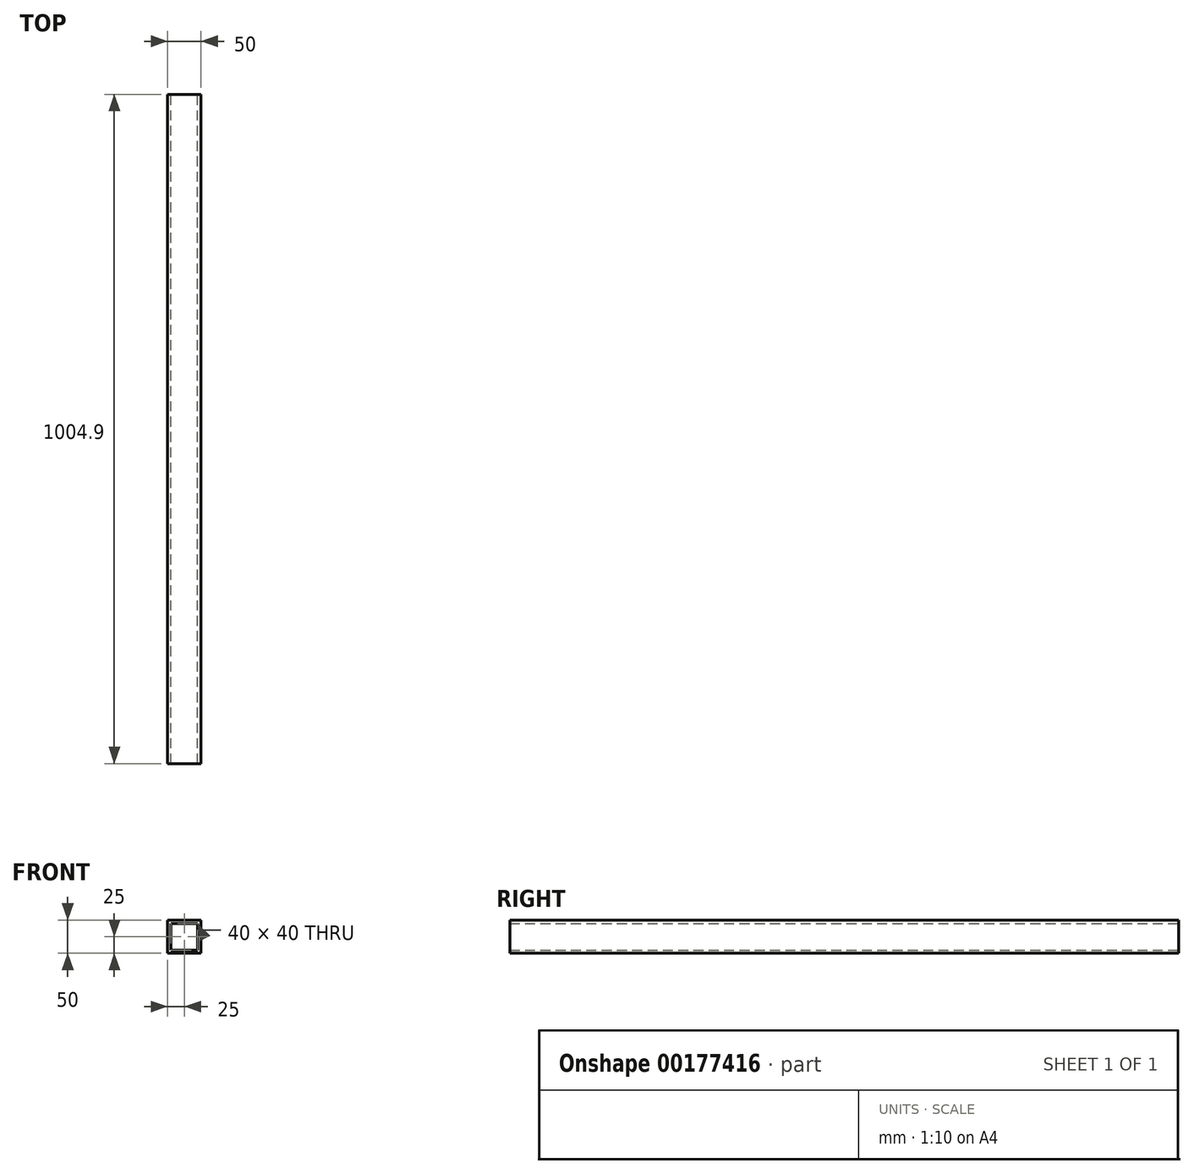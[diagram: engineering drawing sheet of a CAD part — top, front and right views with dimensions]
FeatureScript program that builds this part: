
annotation { "Feature Type Name" : "Feature", "Feature Type Description" : "" }
export const myFeature = defineFeature(function(context is Context, id is Id, definition is map)
    precondition{}
    {
        {
            var Q0;
            Q0=qCreatedBy(makeId("Front.planeOp"),FACE);
            var sketch = newSketch(context, id + "F0", { "sketchPlane" : qUnion([Q0])});
            skLineSegment(sketch, "E0.bottom", {"start": v(25, -25) * mm, "end": v(-25, -25) * mm});
            skLineSegment(sketch, "E0.top", {"start": v(25, 25) * mm, "end": v(-25, 25) * mm});
            skLineSegment(sketch, "E0.left", {"start": v(25, -25) * mm, "end": v(25, 25) * mm});
            skLineSegment(sketch, "E0.right", {"start": v(-25, -25) * mm, "end": v(-25, 25) * mm});
            skPoint(sketch, "E0.middle", {"position": v(0, 0) * mm});
            skLineSegment(sketch, "E1.0", {"start": v(20, 20) * mm, "end": v(-20, 20) * mm});
            skLineSegment(sketch, "E1.1", {"start": v(20, -20) * mm, "end": v(20, 20) * mm});
            skLineSegment(sketch, "E1.2", {"start": v(20, -20) * mm, "end": v(-20, -20) * mm});
            skLineSegment(sketch, "E1.3", {"start": v(-20, -20) * mm, "end": v(-20, 20) * mm});
            skSolve(sketch);
        }
        {
            var Q0;
            Q0=makeQuery(id+"F0.imprint","IMPRINT",FACE,{"disambiguationData":[TD([[makeQuery(id+"F0.imprint","IMPRINT",EDGE,{"derivedFrom":sQuery(id+"F0.wireOp",EDGE,"E0.bottom")}),-1.0]])]});
            extrude(context, id + "F1", {"entities" : qUnion([Q0]), "depth" : 1004.9 * mm});
        }
    });
